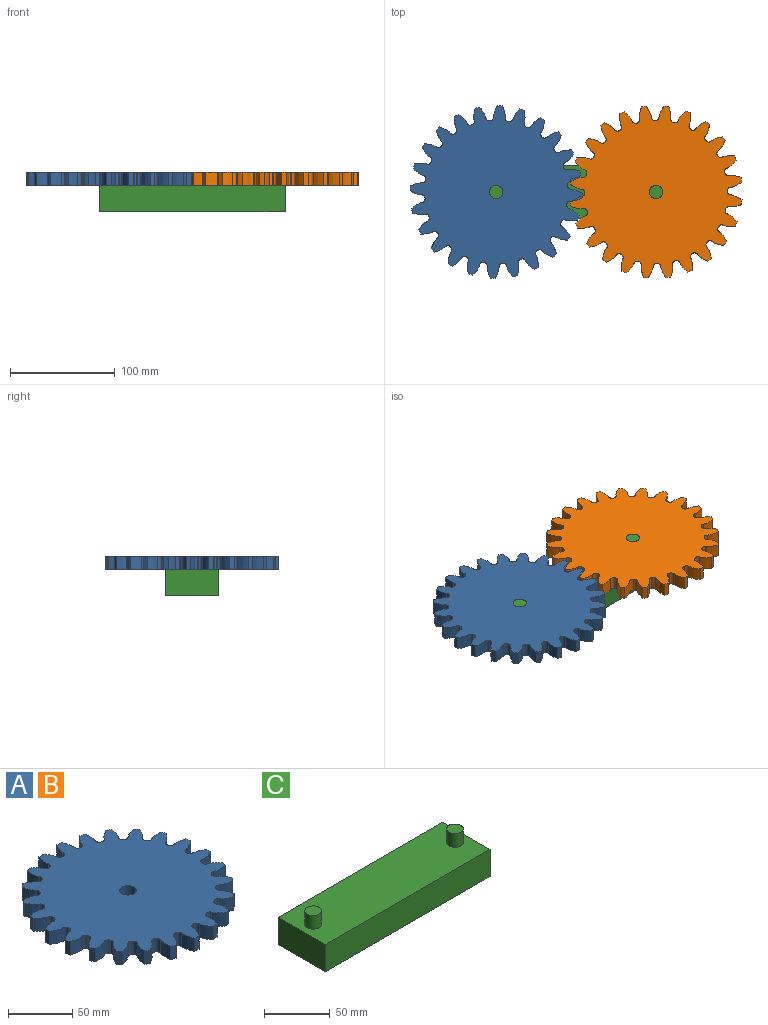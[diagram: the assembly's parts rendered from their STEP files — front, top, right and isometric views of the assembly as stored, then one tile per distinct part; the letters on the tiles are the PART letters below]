
ASSEMBLY  parts=3 mates=2
PART A: 195 faces, bbox 164.9x164.9x12.7 mm
  f0: cylinder r=68.43mm len=12.7mm, axis (0,0,-1), area 10.8mm2, adj f24,f25,f130,f137
  f1: cylinder r=68.43mm len=12.7mm, axis (0,0,-1), area 10.8mm2, adj f24,f25,f123,f129
  f2: cylinder r=68.43mm len=12.7mm, axis (0,0,-1), area 10.8mm2, adj f24,f25,f116,f122
  f3: cylinder r=68.43mm len=12.7mm, axis (0,0,-1), area 10.8mm2, adj f24,f25,f109,f115
  f4: cylinder r=68.43mm len=12.7mm, axis (0,0,-1), area 10.8mm2, adj f24,f25,f102,f108
  f5: cylinder r=68.43mm len=12.7mm, axis (0,0,-1), area 10.8mm2, adj f24,f25,f95,f101
  f6: cylinder r=68.43mm len=12.7mm, axis (0,0,-1), area 10.8mm2, adj f24,f25,f88,f94
  f7: cylinder r=68.43mm len=12.7mm, axis (0,0,-1), area 10.8mm2, adj f24,f25,f81,f87
  f8: cylinder r=68.43mm len=12.7mm, axis (0,0,-1), area 10.8mm2, adj f24,f25,f74,f80
  f9: cylinder r=68.43mm len=12.7mm, axis (0,0,-1), area 10.8mm2, adj f24,f25,f67,f73
  f10: cylinder r=68.43mm len=12.7mm, axis (0,0,-1), area 10.8mm2, adj f24,f25,f60,f66
  f11: cylinder r=68.43mm len=12.7mm, axis (0,0,-1), area 10.8mm2, adj f24,f25,f53,f59
  f12: cylinder r=68.43mm len=12.7mm, axis (0,0,-1), area 10.8mm2, adj f24,f25,f46,f52
  f13: cylinder r=68.43mm len=12.7mm, axis (0,0,-1), area 10.8mm2, adj f24,f25,f39,f45
  f14: cylinder r=68.43mm len=12.7mm, axis (0,0,-1), area 10.8mm2, adj f24,f25,f38,f193
  f15: cylinder r=68.43mm len=12.7mm, axis (0,0,-1), area 10.8mm2, adj f24,f25,f186,f192
  f16: cylinder r=68.43mm len=12.7mm, axis (0,0,-1), area 10.8mm2, adj f24,f25,f179,f185
  f17: cylinder r=68.43mm len=12.7mm, axis (0,0,-1), area 10.8mm2, adj f24,f25,f172,f178
  f18: cylinder r=68.43mm len=12.7mm, axis (0,0,-1), area 10.8mm2, adj f24,f25,f151,f158
  f19: cylinder r=68.43mm len=12.7mm, axis (0,0,-1), area 10.8mm2, adj f24,f25,f165,f171
  f20: cylinder r=68.43mm len=12.7mm, axis (0,0,-1), area 10.8mm2, adj f24,f25,f32,f164
  f21: cylinder r=68.43mm len=12.7mm, axis (0,0,-1), area 10.8mm2, adj f24,f25,f31,f157
  f22: cylinder r=68.43mm len=12.7mm, axis (0,0,-1), area 10.8mm2, adj f24,f25,f136,f144
  f23: cylinder r=68.43mm len=12.7mm, axis (0,0,-1), area 10.8mm2, adj f24,f25,f143,f150
  f24: plane 164.91x164.91mm, normal (0,0,1), area 17893.1mm2, adj f0,f1,f2,f3,f4,f5,f6,f7
  f25: plane 164.91x164.91mm, normal (0,0,-1), area 17893.1mm2, adj f0,f1,f2,f3,f4,f5,f6,f7
  f26: plane 12.7x0.07mm, normal (0.99,-0.16,0), area 0.9mm2, adj f24,f25,f27,f32
  f27: extruded ~12.7x11.39mm, area 149.5mm2, adj f24,f25,f26,f28
  f28: cylinder r=82.55mm len=12.7mm, axis (0,0,-1), area 58.2mm2, adj f24,f25,f27,f29
  f29: extruded ~12.7x10.83mm, area 149.5mm2, adj f24,f25,f28,f30
  f30: plane 12.7x0.07mm, normal (-1,0,0), area 0.9mm2, adj f24,f25,f29,f31
  f31: cylinder r=3.17mm len=12.7mm, axis (0,0,-1), area 61.5mm2, adj f21,f24,f25,f30
  f32: cylinder r=3.17mm len=12.7mm, axis (0,0,-1), area 61.5mm2, adj f20,f24,f25,f26
  f33: plane 12.7x0.07mm, normal (-0.16,-0.99,0), area 0.9mm2, adj f24,f25,f34,f39
  f34: extruded ~12.7x11.39mm, area 149.5mm2, adj f24,f25,f33,f35
  f35: cylinder r=82.55mm len=12.7mm, axis (0,0,-1), area 58.2mm2, adj f24,f25,f34,f36
  f36: extruded ~12.7x10.83mm, area 149.5mm2, adj f24,f25,f35,f37
  f37: plane 12.7x0.07mm, normal (0,1,0), area 0.9mm2, adj f24,f25,f36,f38
  f38: cylinder r=3.17mm len=12.7mm, axis (0,0,-1), area 61.5mm2, adj f14,f24,f25,f37
  f39: cylinder r=3.17mm len=12.7mm, axis (0,0,-1), area 61.5mm2, adj f13,f24,f25,f33
  f40: plane 12.7x0.06mm, normal (-0.41,-0.91,0), area 0.9mm2, adj f24,f25,f41,f46
  f41: extruded ~12.7x11.66mm, area 149.5mm2, adj f24,f25,f40,f42
  f42: cylinder r=82.55mm len=12.7mm, axis (0,0,-1), area 58.2mm2, adj f24,f25,f41,f43
  f43: extruded ~12.7x9.34mm, area 149.5mm2, adj f24,f25,f42,f44
  f44: plane 12.7x0.07mm, normal (0.26,0.97,0), area 0.9mm2, adj f24,f25,f43,f45
  f45: cylinder r=3.17mm len=12.7mm, axis (0,0,-1), area 61.5mm2, adj f13,f24,f25,f44
  f46: cylinder r=3.17mm len=12.7mm, axis (0,0,-1), area 61.5mm2, adj f12,f24,f25,f40
  f47: plane 12.7x0.05mm, normal (-0.63,-0.77,0), area 0.9mm2, adj f24,f25,f48,f53
  f48: extruded ~12.7x11.13mm, area 149.5mm2, adj f24,f25,f47,f49
  f49: cylinder r=82.55mm len=12.7mm, axis (0,0,-1), area 58.2mm2, adj f24,f25,f48,f50
  f50: extruded ~12.7x9.17mm, area 149.5mm2, adj f24,f25,f49,f51
  f51: plane 12.7x0.06mm, normal (0.5,0.87,0), area 0.9mm2, adj f24,f25,f50,f52
  f52: cylinder r=3.17mm len=12.7mm, axis (0,0,-1), area 61.5mm2, adj f12,f24,f25,f51
  f53: cylinder r=3.17mm len=12.7mm, axis (0,0,-1), area 61.5mm2, adj f11,f24,f25,f47
  f54: plane 12.7x0.06mm, normal (-0.81,-0.58,0), area 0.9mm2, adj f24,f25,f55,f60
  f55: extruded ~12.7x9.85mm, area 149.5mm2, adj f24,f25,f54,f56
  f56: cylinder r=82.55mm len=12.7mm, axis (0,0,-1), area 58.2mm2, adj f24,f25,f55,f57
  f57: extruded ~12.7x10.73mm, area 149.5mm2, adj f24,f25,f56,f58
  f58: plane 12.7x0.05mm, normal (0.71,0.71,0), area 0.9mm2, adj f24,f25,f57,f59
  f59: cylinder r=3.17mm len=12.7mm, axis (0,0,-1), area 61.5mm2, adj f11,f24,f25,f58
  f60: cylinder r=3.17mm len=12.7mm, axis (0,0,-1), area 61.5mm2, adj f10,f24,f25,f54
  f61: plane 12.7x0.07mm, normal (-0.93,-0.36,0), area 0.9mm2, adj f24,f25,f62,f67
  f62: extruded ~12.7x8.59mm, area 149.5mm2, adj f24,f25,f61,f63
  f63: cylinder r=82.55mm len=12.7mm, axis (0,0,-1), area 58.2mm2, adj f24,f25,f62,f64
  f64: extruded ~12.7x11.55mm, area 149.5mm2, adj f24,f25,f63,f65
  f65: plane 12.7x0.06mm, normal (0.87,0.5,0), area 0.9mm2, adj f24,f25,f64,f66
  f66: cylinder r=3.17mm len=12.7mm, axis (0,0,-1), area 61.5mm2, adj f10,f24,f25,f65
  f67: cylinder r=3.17mm len=12.7mm, axis (0,0,-1), area 61.5mm2, adj f9,f24,f25,f61
  f68: plane 12.7x0.07mm, normal (-0.99,-0.1,0), area 0.9mm2, adj f24,f25,f69,f74
  f69: extruded ~12.7x10.34mm, area 149.5mm2, adj f24,f25,f68,f70
  f70: cylinder r=82.55mm len=12.7mm, axis (0,0,-1), area 58.2mm2, adj f24,f25,f69,f71
  f71: extruded ~12.7x11.58mm, area 149.5mm2, adj f24,f25,f70,f72
  f72: plane 12.7x0.07mm, normal (0.97,0.26,0), area 0.9mm2, adj f24,f25,f71,f73
  f73: cylinder r=3.17mm len=12.7mm, axis (0,0,-1), area 61.5mm2, adj f9,f24,f25,f72
  f74: cylinder r=3.17mm len=12.7mm, axis (0,0,-1), area 61.5mm2, adj f8,f24,f25,f68
  f75: plane 12.7x0.07mm, normal (-0.99,0.16,0), area 0.9mm2, adj f24,f25,f76,f81
  f76: extruded ~12.7x11.39mm, area 149.5mm2, adj f24,f25,f75,f77
  f77: cylinder r=82.55mm len=12.7mm, axis (0,0,-1), area 58.2mm2, adj f24,f25,f76,f78
  f78: extruded ~12.7x10.83mm, area 149.5mm2, adj f24,f25,f77,f79
  f79: plane 12.7x0.07mm, normal (1,0,0), area 0.9mm2, adj f24,f25,f78,f80
  f80: cylinder r=3.17mm len=12.7mm, axis (0,0,-1), area 61.5mm2, adj f8,f24,f25,f79
  f81: cylinder r=3.17mm len=12.7mm, axis (0,0,-1), area 61.5mm2, adj f7,f24,f25,f75
  f82: plane 12.7x0.06mm, normal (-0.91,0.41,0), area 0.9mm2, adj f24,f25,f83,f88
  f83: extruded ~12.7x11.66mm, area 149.5mm2, adj f24,f25,f82,f84
  f84: cylinder r=82.55mm len=12.7mm, axis (0,0,-1), area 58.2mm2, adj f24,f25,f83,f85
  f85: extruded ~12.7x9.34mm, area 149.5mm2, adj f24,f25,f84,f86
  f86: plane 12.7x0.07mm, normal (0.97,-0.26,0), area 0.9mm2, adj f24,f25,f85,f87
  f87: cylinder r=3.17mm len=12.7mm, axis (0,0,-1), area 61.5mm2, adj f7,f24,f25,f86
  f88: cylinder r=3.17mm len=12.7mm, axis (0,0,-1), area 61.5mm2, adj f6,f24,f25,f82
  f89: plane 12.7x0.05mm, normal (-0.77,0.63,0), area 0.9mm2, adj f24,f25,f90,f95
  f90: extruded ~12.7x11.13mm, area 149.5mm2, adj f24,f25,f89,f91
  f91: cylinder r=82.55mm len=12.7mm, axis (0,0,-1), area 58.2mm2, adj f24,f25,f90,f92
  f92: extruded ~12.7x9.17mm, area 149.5mm2, adj f24,f25,f91,f93
  f93: plane 12.7x0.06mm, normal (0.87,-0.5,0), area 0.9mm2, adj f24,f25,f92,f94
  f94: cylinder r=3.17mm len=12.7mm, axis (0,0,-1), area 61.5mm2, adj f6,f24,f25,f93
  f95: cylinder r=3.17mm len=12.7mm, axis (0,0,-1), area 61.5mm2, adj f5,f24,f25,f89
  f96: plane 12.7x0.06mm, normal (-0.58,0.81,0), area 0.9mm2, adj f24,f25,f97,f102
  f97: extruded ~12.7x9.85mm, area 149.5mm2, adj f24,f25,f96,f98
  f98: cylinder r=82.55mm len=12.7mm, axis (0,0,-1), area 58.2mm2, adj f24,f25,f97,f99
  f99: extruded ~12.7x10.73mm, area 149.5mm2, adj f24,f25,f98,f100
  f100: plane 12.7x0.05mm, normal (0.71,-0.71,0), area 0.9mm2, adj f24,f25,f99,f101
  f101: cylinder r=3.17mm len=12.7mm, axis (0,0,-1), area 61.5mm2, adj f5,f24,f25,f100
  f102: cylinder r=3.17mm len=12.7mm, axis (0,0,-1), area 61.5mm2, adj f4,f24,f25,f96
  f103: plane 12.7x0.07mm, normal (-0.36,0.93,0), area 0.9mm2, adj f24,f25,f104,f109
  f104: extruded ~12.7x8.59mm, area 149.5mm2, adj f24,f25,f103,f105
  f105: cylinder r=82.55mm len=12.7mm, axis (0,0,-1), area 58.2mm2, adj f24,f25,f104,f106
  f106: extruded ~12.7x11.55mm, area 149.5mm2, adj f24,f25,f105,f107
  f107: plane 12.7x0.06mm, normal (0.5,-0.87,0), area 0.9mm2, adj f24,f25,f106,f108
  f108: cylinder r=3.17mm len=12.7mm, axis (0,0,-1), area 61.5mm2, adj f4,f24,f25,f107
  f109: cylinder r=3.17mm len=12.7mm, axis (0,0,-1), area 61.5mm2, adj f3,f24,f25,f103
  f110: plane 12.7x0.07mm, normal (-0.1,0.99,0), area 0.9mm2, adj f24,f25,f111,f116
  f111: extruded ~12.7x10.34mm, area 149.5mm2, adj f24,f25,f110,f112
  f112: cylinder r=82.55mm len=12.7mm, axis (0,0,-1), area 58.2mm2, adj f24,f25,f111,f113
  f113: extruded ~12.7x11.58mm, area 149.5mm2, adj f24,f25,f112,f114
  f114: plane 12.7x0.07mm, normal (0.26,-0.97,0), area 0.9mm2, adj f24,f25,f113,f115
  f115: cylinder r=3.17mm len=12.7mm, axis (0,0,-1), area 61.5mm2, adj f3,f24,f25,f114
  f116: cylinder r=3.17mm len=12.7mm, axis (0,0,-1), area 61.5mm2, adj f2,f24,f25,f110
  f117: plane 12.7x0.07mm, normal (0.16,0.99,0), area 0.9mm2, adj f24,f25,f118,f123
  f118: extruded ~12.7x11.39mm, area 149.5mm2, adj f24,f25,f117,f119
  f119: cylinder r=82.55mm len=12.7mm, axis (0,0,-1), area 58.2mm2, adj f24,f25,f118,f120
  f120: extruded ~12.7x10.83mm, area 149.5mm2, adj f24,f25,f119,f121
  f121: plane 12.7x0.07mm, normal (0,-1,0), area 0.9mm2, adj f24,f25,f120,f122
  f122: cylinder r=3.17mm len=12.7mm, axis (0,0,-1), area 61.5mm2, adj f2,f24,f25,f121
  f123: cylinder r=3.17mm len=12.7mm, axis (0,0,-1), area 61.5mm2, adj f1,f24,f25,f117
  f124: plane 12.7x0.06mm, normal (0.41,0.91,0), area 0.9mm2, adj f24,f25,f125,f130
  f125: extruded ~12.7x11.66mm, area 149.5mm2, adj f24,f25,f124,f126
  f126: cylinder r=82.55mm len=12.7mm, axis (0,0,-1), area 58.2mm2, adj f24,f25,f125,f127
  f127: extruded ~12.7x9.34mm, area 149.5mm2, adj f24,f25,f126,f128
  f128: plane 12.7x0.07mm, normal (-0.26,-0.97,0), area 0.9mm2, adj f24,f25,f127,f129
  f129: cylinder r=3.17mm len=12.7mm, axis (0,0,-1), area 61.5mm2, adj f1,f24,f25,f128
  f130: cylinder r=3.17mm len=12.7mm, axis (0,0,-1), area 61.5mm2, adj f0,f24,f25,f124
  f131: plane 12.7x0.05mm, normal (0.63,0.77,0), area 0.9mm2, adj f24,f25,f132,f136
  f132: extruded ~12.7x11.13mm, area 149.5mm2, adj f24,f25,f131,f133
  f133: cylinder r=82.55mm len=12.7mm, axis (0,0,-1), area 58.2mm2, adj f24,f25,f132,f134
  f134: extruded ~12.7x9.17mm, area 149.5mm2, adj f24,f25,f133,f135
  f135: plane 12.7x0.06mm, normal (-0.5,-0.87,0), area 0.9mm2, adj f24,f25,f134,f137
  f136: cylinder r=3.17mm len=12.7mm, axis (0,0,-1), area 61.5mm2, adj f22,f24,f25,f131
  f137: cylinder r=3.17mm len=12.7mm, axis (0,0,-1), area 61.5mm2, adj f0,f24,f25,f135
  f138: plane 12.7x0.06mm, normal (0.81,0.58,0), area 0.9mm2, adj f24,f25,f139,f143
  f139: extruded ~12.7x9.85mm, area 149.5mm2, adj f24,f25,f138,f140
  f140: cylinder r=82.55mm len=12.7mm, axis (0,0,-1), area 58.2mm2, adj f24,f25,f139,f141
  f141: extruded ~12.7x10.73mm, area 149.5mm2, adj f24,f25,f140,f142
  f142: plane 12.7x0.05mm, normal (-0.71,-0.71,0), area 0.9mm2, adj f24,f25,f141,f144
  f143: cylinder r=3.17mm len=12.7mm, axis (0,0,-1), area 61.5mm2, adj f23,f24,f25,f138
  f144: cylinder r=3.17mm len=12.7mm, axis (0,0,-1), area 61.5mm2, adj f22,f24,f25,f142
  f145: plane 12.7x0.07mm, normal (0.93,0.36,0), area 0.9mm2, adj f24,f25,f146,f151
  f146: extruded ~12.7x8.59mm, area 149.5mm2, adj f24,f25,f145,f147
  f147: cylinder r=82.55mm len=12.7mm, axis (0,0,-1), area 58.2mm2, adj f24,f25,f146,f148
  f148: extruded ~12.7x11.55mm, area 149.5mm2, adj f24,f25,f147,f149
  f149: plane 12.7x0.06mm, normal (-0.87,-0.5,0), area 0.9mm2, adj f24,f25,f148,f150
  f150: cylinder r=3.17mm len=12.7mm, axis (0,0,-1), area 61.5mm2, adj f23,f24,f25,f149
  f151: cylinder r=3.17mm len=12.7mm, axis (0,0,-1), area 61.5mm2, adj f18,f24,f25,f145
  f152: plane 12.7x0.07mm, normal (0.99,0.1,0), area 0.9mm2, adj f24,f25,f153,f157
  f153: extruded ~12.7x10.34mm, area 149.5mm2, adj f24,f25,f152,f154
  f154: cylinder r=82.55mm len=12.7mm, axis (0,0,-1), area 58.2mm2, adj f24,f25,f153,f155
  f155: extruded ~12.7x11.58mm, area 149.5mm2, adj f24,f25,f154,f156
  f156: plane 12.7x0.07mm, normal (-0.97,-0.26,0), area 0.9mm2, adj f24,f25,f155,f158
  f157: cylinder r=3.17mm len=12.7mm, axis (0,0,-1), area 61.5mm2, adj f21,f24,f25,f152
  f158: cylinder r=3.17mm len=12.7mm, axis (0,0,-1), area 61.5mm2, adj f18,f24,f25,f156
  f159: plane 12.7x0.06mm, normal (0.91,-0.41,0), area 0.9mm2, adj f24,f25,f160,f165
  f160: extruded ~12.7x11.66mm, area 149.5mm2, adj f24,f25,f159,f161
  f161: cylinder r=82.55mm len=12.7mm, axis (0,0,-1), area 58.2mm2, adj f24,f25,f160,f162
  f162: extruded ~12.7x9.34mm, area 149.5mm2, adj f24,f25,f161,f163
  f163: plane 12.7x0.07mm, normal (-0.97,0.26,0), area 0.9mm2, adj f24,f25,f162,f164
  f164: cylinder r=3.17mm len=12.7mm, axis (0,0,-1), area 61.5mm2, adj f20,f24,f25,f163
  f165: cylinder r=3.17mm len=12.7mm, axis (0,0,-1), area 61.5mm2, adj f19,f24,f25,f159
  f166: plane 12.7x0.05mm, normal (0.77,-0.63,0), area 0.9mm2, adj f24,f25,f167,f172
  f167: extruded ~12.7x11.13mm, area 149.5mm2, adj f24,f25,f166,f168
  f168: cylinder r=82.55mm len=12.7mm, axis (0,0,-1), area 58.2mm2, adj f24,f25,f167,f169
  f169: extruded ~12.7x9.17mm, area 149.5mm2, adj f24,f25,f168,f170
  f170: plane 12.7x0.06mm, normal (-0.87,0.5,0), area 0.9mm2, adj f24,f25,f169,f171
  f171: cylinder r=3.17mm len=12.7mm, axis (0,0,-1), area 61.5mm2, adj f19,f24,f25,f170
  f172: cylinder r=3.17mm len=12.7mm, axis (0,0,-1), area 61.5mm2, adj f17,f24,f25,f166
  f173: plane 12.7x0.06mm, normal (0.58,-0.81,0), area 0.9mm2, adj f24,f25,f174,f179
  f174: extruded ~12.7x9.85mm, area 149.5mm2, adj f24,f25,f173,f175
  f175: cylinder r=82.55mm len=12.7mm, axis (0,0,-1), area 58.2mm2, adj f24,f25,f174,f176
  f176: extruded ~12.7x10.73mm, area 149.5mm2, adj f24,f25,f175,f177
  f177: plane 12.7x0.05mm, normal (-0.71,0.71,0), area 0.9mm2, adj f24,f25,f176,f178
  f178: cylinder r=3.17mm len=12.7mm, axis (0,0,-1), area 61.5mm2, adj f17,f24,f25,f177
  f179: cylinder r=3.17mm len=12.7mm, axis (0,0,-1), area 61.5mm2, adj f16,f24,f25,f173
  f180: plane 12.7x0.07mm, normal (0.36,-0.93,0), area 0.9mm2, adj f24,f25,f181,f186
  f181: extruded ~12.7x8.59mm, area 149.5mm2, adj f24,f25,f180,f182
  f182: cylinder r=82.55mm len=12.7mm, axis (0,0,-1), area 58.2mm2, adj f24,f25,f181,f183
  f183: extruded ~12.7x11.55mm, area 149.5mm2, adj f24,f25,f182,f184
  f184: plane 12.7x0.06mm, normal (-0.5,0.87,0), area 0.9mm2, adj f24,f25,f183,f185
  f185: cylinder r=3.17mm len=12.7mm, axis (0,0,-1), area 61.5mm2, adj f16,f24,f25,f184
  f186: cylinder r=3.17mm len=12.7mm, axis (0,0,-1), area 61.5mm2, adj f15,f24,f25,f180
  f187: plane 12.7x0.07mm, normal (0.1,-0.99,0), area 0.9mm2, adj f24,f25,f188,f193
  f188: extruded ~12.7x10.34mm, area 149.5mm2, adj f24,f25,f187,f189
  f189: cylinder r=82.55mm len=12.7mm, axis (0,0,-1), area 58.2mm2, adj f24,f25,f188,f190
  f190: extruded ~12.7x11.58mm, area 149.5mm2, adj f24,f25,f189,f191
  f191: plane 12.7x0.07mm, normal (-0.26,0.97,0), area 0.9mm2, adj f24,f25,f190,f192
  f192: cylinder r=3.17mm len=12.7mm, axis (0,0,-1), area 61.5mm2, adj f15,f24,f25,f191
  f193: cylinder r=3.17mm len=12.7mm, axis (0,0,-1), area 61.5mm2, adj f14,f24,f25,f187
  f194: cylinder r=6.35mm len=12.7mm, axis (0,0,-1), area 506.7mm2, adj f24,f25
PART B: same geometry as A
PART C: 10 faces, bbox 177.8x50.8x38.1 mm
  f0: plane 50.8x25.4mm, normal (-1,0,0), area 1290.3mm2, adj f1,f3,f4,f5
  f1: plane 177.8x25.4mm, normal (0,-1,0), area 4516.1mm2, adj f0,f2,f4,f5
  f2: plane 50.8x25.4mm, normal (1,0,0), area 1290.3mm2, adj f1,f3,f4,f5
  f3: plane 177.8x25.4mm, normal (0,1,0), area 4516.1mm2, adj f0,f2,f4,f5
  f4: plane 177.8x50.8mm, normal (0,0,1), area 8778.9mm2, adj f0,f1,f2,f3,f6,f8
  f5: plane 177.8x50.8mm, normal (0,0,-1), area 9032.2mm2, adj f0,f1,f2,f3
  f6: cylinder r=6.35mm len=12.7mm, axis (0,0,-1), area 506.7mm2, adj f4,f7
  f7: plane 12.7x12.7mm, normal (0,0,1), area 126.7mm2, adj f6
  f8: cylinder r=6.35mm len=12.7mm, axis (0,0,-1), area 506.7mm2, adj f4,f9
  f9: plane 12.7x12.7mm, normal (0,0,1), area 126.7mm2, adj f8
PLACE A rot(axis=(0,0,-1),57.8deg) t=(-76.45,0,25.4)mm
PLACE B rot(axis=(0,0,1),147.8deg) t=(76.45,0,25.4)mm
PLACE C at identity fixed
MATE revolute A.f0 <-> C.f6  axis (0,0,-1) through (-76.45,0,38.1)mm
MATE revolute B.f28 <-> C.f8  axis (0,0,1) through (76.45,0,38.1)mm
